# Revit family: 56217XXX
name_source: partatom
category: Plumbing Fixtures
revit_build: Autodesk Revit 2018 (Build: 20170223_1515(x64)
units: mm (PartAtom-declared; Revit-internal decimal feet)

## family parameters
Cut with Voids When Loaded = No
Host = Face
OmniClass Number = 23.31.17.29
OmniClass Title = Shower Drains
Part Type = Normal
Room Calculation Point = No
Round Connector Dimension = Use Diameter
Shared = No

## types (3) — shared parameters
Default Elevation = 1219 mm
Description = RainDrain Match Plus Finish set shower drain 1000 with height adjustable frame
Manufacturer = Hansgrohe
Material 1 = Hansgrohe - Plastic - Black
Model = 56217XXX
Product Guid = b02c80dc-bedb-4b61-b684-d92b8da452ab
Product Page URL = https://pro.hansgrohe.com
Product data url = https://bimobject.com
URL = https://www.hansgrohe.com
Version = 1
zero-valued in all types: Edition number

## per-type parameters (varying)
| type | Material |
| 000 Chrome | Hansgrohe - Metal - 000 Chrome |
| 670 Matte Black | Hansgrohe - Metal - 670 Matte Black |
| 800 Stainless Steel Optic | Hansgrohe - Metal - 800 Stainless Steel Optic |

## geometry (parser evidence)
native form markers: Sweep x5
no freeform markers — native parametric forms only
